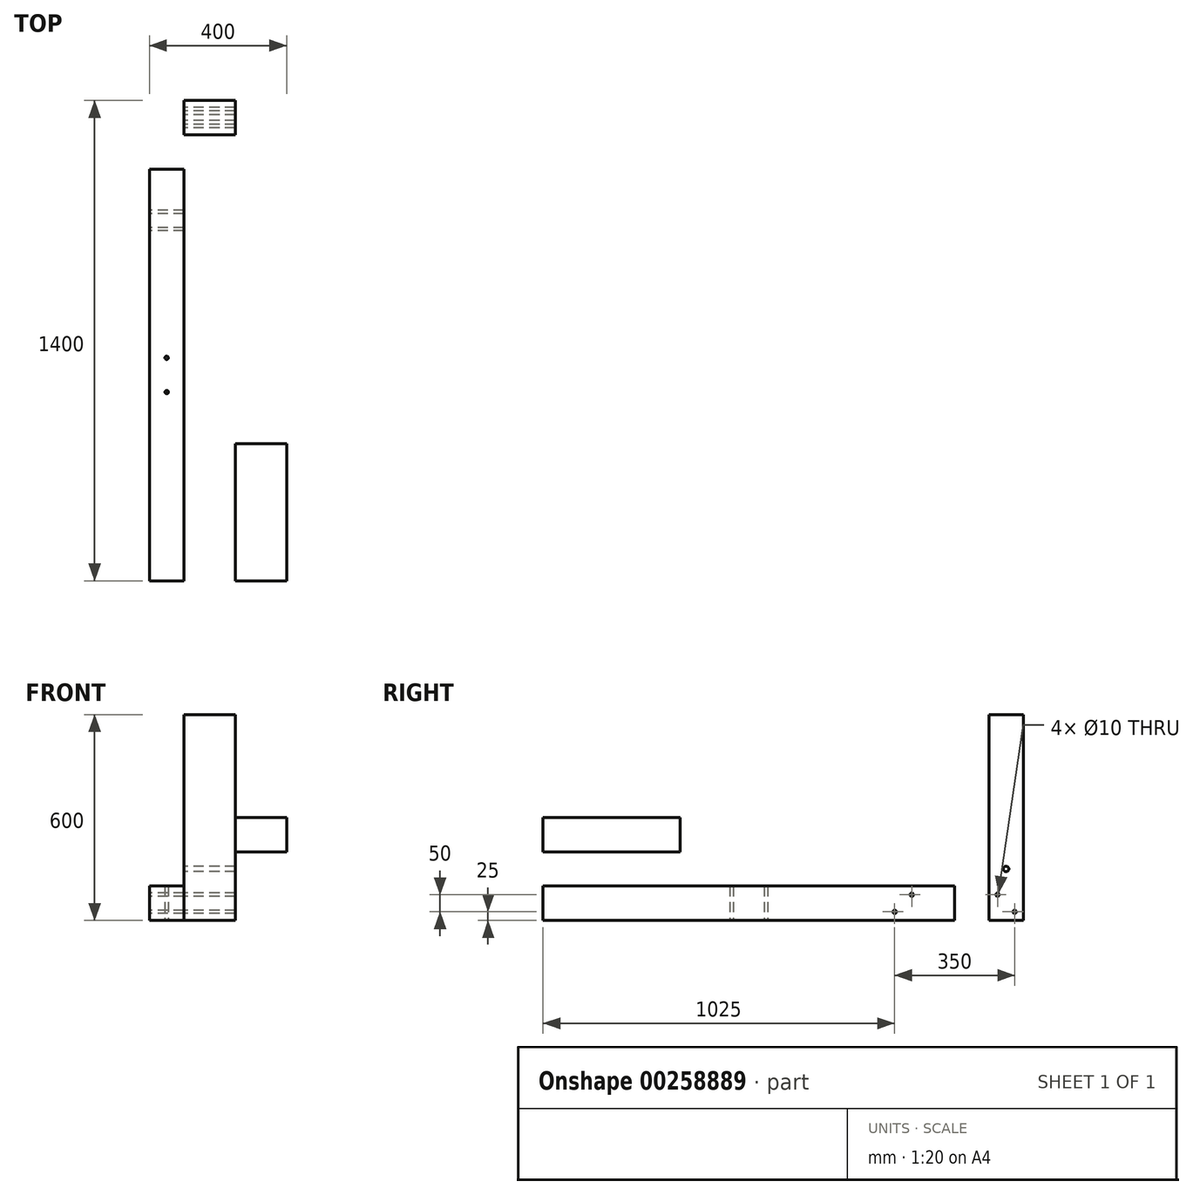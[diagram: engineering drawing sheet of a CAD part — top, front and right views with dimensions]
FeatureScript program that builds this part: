
annotation { "Feature Type Name" : "Feature", "Feature Type Description" : "" }
export const myFeature = defineFeature(function(context is Context, id is Id, definition is map)
    precondition{}
    {
        {
            var Q0;
            Q0=qCreatedBy(makeId("Right.planeOp"),FACE);
            var sketch = newSketch(context, id + "F0", { "sketchPlane" : qUnion([Q0])});
            skLineSegment(sketch, "E0.bottom", {"start": v(-200, 0) * mm, "end": v(-1400, 0) * mm});
            skLineSegment(sketch, "E0.top", {"start": v(-200, 100) * mm, "end": v(-1400, 100) * mm});
            skLineSegment(sketch, "E0.left", {"start": v(-200, 0) * mm, "end": v(-200, 100) * mm});
            skLineSegment(sketch, "E0.right", {"start": v(-1400, 0) * mm, "end": v(-1400, 100) * mm});
            skLineSegment(sketch, "E1.bottom", {"start": v(-1400, 300) * mm, "end": v(-1000, 300) * mm});
            skLineSegment(sketch, "E1.top", {"start": v(-1400, 200) * mm, "end": v(-1000, 200) * mm});
            skLineSegment(sketch, "E1.left", {"start": v(-1400, 300) * mm, "end": v(-1400, 200) * mm});
            skLineSegment(sketch, "E1.right", {"start": v(-1000, 300) * mm, "end": v(-1000, 200) * mm});
            skLineSegment(sketch, "E2.bottom", {"start": v(-100, 0) * mm, "end": v(0, 0) * mm});
            skLineSegment(sketch, "E2.top", {"start": v(-100, 650) * mm, "end": v(0, 650) * mm});
            skLineSegment(sketch, "E2.left", {"start": v(-100, 0) * mm, "end": v(-100, 650) * mm});
            skLineSegment(sketch, "E2.right", {"start": v(0, 0) * mm, "end": v(0, 650) * mm});
            skLineSegment(sketch, "E3", {"start": v(-400, 100) * mm, "end": v(-400, 0) * mm, "construction": true});
            skLineSegment(sketch, "E4", {"start": v(-300, 100) * mm, "end": v(-300, 0) * mm, "construction": true});
            skLineSegment(sketch, "E5", {"start": v(-1200, 300) * mm, "end": v(-1200, 927.2) * mm, "construction": true});
            skLineSegment(sketch, "E6", {"start": v(-300, 100) * mm, "end": v(-400, 0) * mm, "construction": true});
            skLineSegment(sketch, "E7.bottom", {"start": v(-325, 75) * mm, "end": v(-375, 75) * mm, "construction": true});
            skLineSegment(sketch, "E7.top", {"start": v(-325, 25) * mm, "end": v(-375, 25) * mm, "construction": true});
            skLineSegment(sketch, "E7.left", {"start": v(-325, 75) * mm, "end": v(-325, 25) * mm, "construction": true});
            skLineSegment(sketch, "E7.right", {"start": v(-375, 75) * mm, "end": v(-375, 25) * mm, "construction": true});
            skPoint(sketch, "E7.middle", {"position": v(-350, 50) * mm});
            skLineSegment(sketch, "E8.bottom", {"start": v(-365, 35) * mm, "end": v(-385, 35) * mm});
            skLineSegment(sketch, "E8.top", {"start": v(-365, 15) * mm, "end": v(-385, 15) * mm});
            skLineSegment(sketch, "E8.left", {"start": v(-365, 35) * mm, "end": v(-365, 15) * mm});
            skLineSegment(sketch, "E8.right", {"start": v(-385, 35) * mm, "end": v(-385, 15) * mm});
            skPoint(sketch, "E8.middle", {"position": v(-375, 25) * mm});
            skLineSegment(sketch, "E9.bottom", {"start": v(-335, 65) * mm, "end": v(-315, 65) * mm});
            skLineSegment(sketch, "E9.top", {"start": v(-335, 85) * mm, "end": v(-315, 85) * mm});
            skLineSegment(sketch, "E9.left", {"start": v(-335, 65) * mm, "end": v(-335, 85) * mm});
            skLineSegment(sketch, "E9.right", {"start": v(-315, 65) * mm, "end": v(-315, 85) * mm});
            skPoint(sketch, "E9.middle", {"position": v(-325, 75) * mm});
            skCircle(sketch, "E10", {"center": v(-375, 25) * mm, "radius": 5 * mm});
            skCircle(sketch, "E11", {"center": v(-325, 75) * mm, "radius": 5 * mm});
            skLineSegment(sketch, "E12", {"start": v(0, 100) * mm, "end": v(-100, 100) * mm, "construction": true});
            skLineSegment(sketch, "E13", {"start": v(0, 0) * mm, "end": v(-100, 100) * mm, "construction": true});
            skLineSegment(sketch, "E14.bottom", {"start": v(-75, 75) * mm, "end": v(-25, 75) * mm, "construction": true});
            skLineSegment(sketch, "E14.top", {"start": v(-75, 25) * mm, "end": v(-25, 25) * mm, "construction": true});
            skLineSegment(sketch, "E14.left", {"start": v(-75, 75) * mm, "end": v(-75, 25) * mm, "construction": true});
            skLineSegment(sketch, "E14.right", {"start": v(-25, 75) * mm, "end": v(-25, 25) * mm, "construction": true});
            skPoint(sketch, "E14.middle", {"position": v(-50, 50) * mm});
            skCircle(sketch, "E15", {"center": v(-25, 25) * mm, "radius": 5 * mm});
            skCircle(sketch, "E16", {"center": v(-75, 75) * mm, "radius": 5 * mm});
            skLineSegment(sketch, "E17", {"start": v(0, 150) * mm, "end": v(-50, 150) * mm, "construction": true});
            skLineSegment(sketch, "E18", {"start": v(-50, 150) * mm, "end": v(-100, 150) * mm, "construction": true});
            skCircle(sketch, "E19", {"center": v(-50, 150) * mm, "radius": 8 * mm});
            skSolve(sketch);
        }
        {
            var Q0;
            Q0=qCreatedBy(makeId("Top.planeOp"),FACE);
            var sketch = newSketch(context, id + "F1", { "sketchPlane" : qUnion([Q0])});
            skLineSegment(sketch, "E20", {"start": v(0, 0) * mm, "end": v(150, 0) * mm});
            skLineSegment(sketch, "E21", {"start": v(150, 0) * mm, "end": v(150, -100) * mm});
            skLineSegment(sketch, "E22", {"start": v(150, -100) * mm, "end": v(0, -100) * mm});
            skLineSegment(sketch, "E23", {"start": v(0, -100) * mm, "end": v(0, 0) * mm});
            skLineSegment(sketch, "E24", {"start": v(0, -200) * mm, "end": v(0, -1400) * mm});
            skLineSegment(sketch, "E25", {"start": v(0, -1400) * mm, "end": v(-100, -1400) * mm});
            skLineSegment(sketch, "E26", {"start": v(-100, -1400) * mm, "end": v(-100, -200) * mm});
            skLineSegment(sketch, "E27", {"start": v(-100, -200) * mm, "end": v(0, -200) * mm});
            skLineSegment(sketch, "E28", {"start": v(150, -1400) * mm, "end": v(150, -1000) * mm});
            skLineSegment(sketch, "E29", {"start": v(150, -1000) * mm, "end": v(300, -1000) * mm});
            skLineSegment(sketch, "E30", {"start": v(300, -1000) * mm, "end": v(300, -1400) * mm});
            skLineSegment(sketch, "E31", {"start": v(300, -1400) * mm, "end": v(150, -1400) * mm});
            skLineSegment(sketch, "E32", {"start": v(-100, -800) * mm, "end": v(-50, -800) * mm, "construction": true});
            skLineSegment(sketch, "E33", {"start": v(-50, -800) * mm, "end": v(-50, -750) * mm, "construction": true});
            skLineSegment(sketch, "E34", {"start": v(-50, -800) * mm, "end": v(0, -800) * mm, "construction": true});
            skLineSegment(sketch, "E35", {"start": v(0, -800) * mm, "end": v(-50, -800) * mm, "construction": true});
            skLineSegment(sketch, "E36", {"start": v(-50, -850) * mm, "end": v(-50, -800) * mm, "construction": true});
            skCircle(sketch, "E37", {"center": v(-50, -750) * mm, "radius": 5 * mm});
            skCircle(sketch, "E38", {"center": v(-50, -850) * mm, "radius": 5 * mm});
            skSolve(sketch);
        }
        {
            var Q0;
            Q0=qCreatedBy(makeId("Front.planeOp"),FACE);
            var sketch = newSketch(context, id + "F2", { "sketchPlane" : qUnion([Q0])});
            skLineSegment(sketch, "E39", {"start": v(0, 0) * mm, "end": v(-100, 0) * mm});
            skLineSegment(sketch, "E40", {"start": v(-100, 0) * mm, "end": v(-100, 100) * mm});
            skLineSegment(sketch, "E41", {"start": v(150, 300) * mm, "end": v(300, 300) * mm});
            skLineSegment(sketch, "E42", {"start": v(300, 300) * mm, "end": v(300, 200) * mm});
            skLineSegment(sketch, "E43", {"start": v(300, 200) * mm, "end": v(150, 200) * mm});
            skLineSegment(sketch, "E44", {"start": v(-100, 100) * mm, "end": v(0, 100) * mm});
            skLineSegment(sketch, "E45", {"start": v(0, 100) * mm, "end": v(0, 600) * mm});
            skLineSegment(sketch, "E46", {"start": v(0, 600) * mm, "end": v(150, 600) * mm});
            skLineSegment(sketch, "E47", {"start": v(150, 600) * mm, "end": v(150, 300) * mm});
            skLineSegment(sketch, "E48", {"start": v(150, 200) * mm, "end": v(150, 0) * mm});
            skLineSegment(sketch, "E49", {"start": v(150, 0) * mm, "end": v(0, 0) * mm});
            skSolve(sketch);
        }
        {
            var Q0;
            Q0=makeQuery(id+"F0.imprint","IMPRINT",FACE,{"disambiguationData":[TD([[makeQuery(id+"F0.imprint","IMPRINT",EDGE,{"derivedFrom":sQuery(id+"F0.wireOp",EDGE,"E1.bottom")}),-1.0]])]});
            var Q1;
            Q1=makeQuery(id+"F0.imprint","IMPRINT",FACE,{"disambiguationData":[TD([[makeQuery(id+"F0.imprint","IMPRINT",EDGE,{"derivedFrom":sQuery(id+"F0.wireOp",EDGE,"E0.bottom")}),-1.0]])]});
            var Q2;
            Q2=makeQuery(id+"F0.imprint","IMPRINT",FACE,{"disambiguationData":[TD([[makeQuery(id+"F0.imprint","IMPRINT",EDGE,{"derivedFrom":sQuery(id+"F0.wireOp",EDGE,"E2.bottom")}),1.0]])]});
            var Q3;
            Q3=makeQuery(id+"F0.imprint","IMPRINT",FACE,{"disambiguationData":[TD([[makeQuery(id+"F0.imprint","IMPRINT",EDGE,{"derivedFrom":sQuery(id+"F0.wireOp",EDGE,"E9.bottom")}),1.0]])]});
            var Q4;
            Q4=makeQuery(id+"F0.imprint","IMPRINT",FACE,{"disambiguationData":[TD([[makeQuery(id+"F0.imprint","IMPRINT",EDGE,{"derivedFrom":sQuery(id+"F0.wireOp",EDGE,"E8.bottom")}),1.0]])]});
            extrude(context, id + "F3", {"entities" : qUnion([Q0, Q1, Q2, Q3, Q4]), "depth" : 846 * mm, "symmetric" : true});
        }
        {
            var Q0;
            Q0 = qSketchRegion(id + "F1", true);
            extrude(context, id + "F4", {"entities" : qUnion([Q0]), "operationType" : NewBodyOperationType.INTERSECT, "depth" : 1000 * mm});
        }
        {
            var Q0;
            Q0 = qSketchRegion(id + "F2", true);
            extrude(context, id + "F5", {"entities" : qUnion([Q0]), "operationType" : NewBodyOperationType.INTERSECT, "depth" : 1520 * mm});
        }
    });
